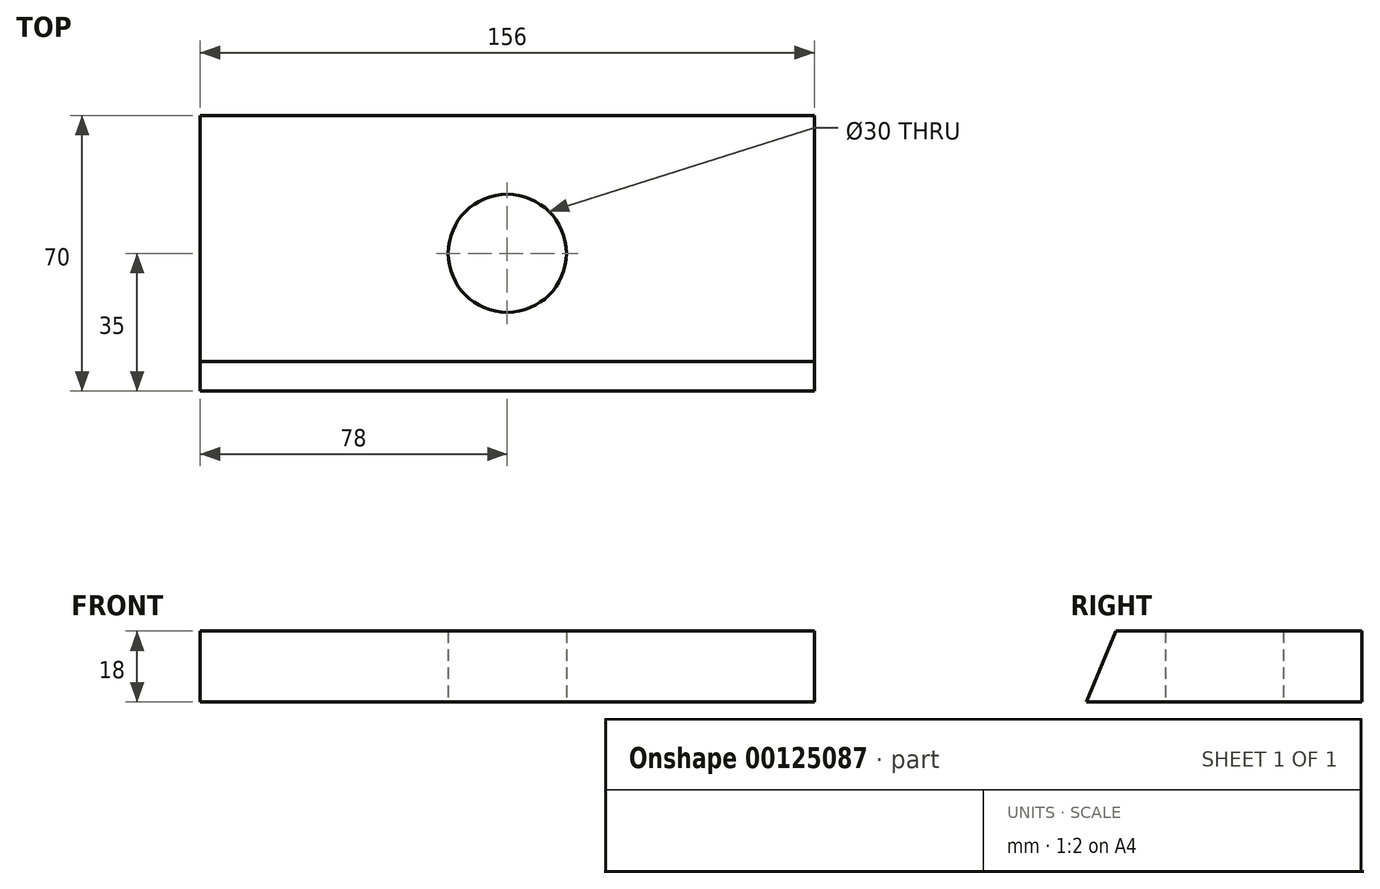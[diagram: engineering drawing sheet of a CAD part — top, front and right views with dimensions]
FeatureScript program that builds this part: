
annotation { "Feature Type Name" : "Feature", "Feature Type Description" : "" }
export const myFeature = defineFeature(function(context is Context, id is Id, definition is map)
    precondition{}
    {
        {
            var Q0;
            Q0=qCreatedBy(makeId("Top.planeOp"),FACE);
            var sketch = newSketch(context, id + "F0", { "sketchPlane" : qUnion([Q0])});
            skLineSegment(sketch, "E0.bottom", {"start": v(0, 0) * mm, "end": v(156, 0) * mm});
            skLineSegment(sketch, "E0.top", {"start": v(0, -70) * mm, "end": v(156, -70) * mm});
            skLineSegment(sketch, "E0.left", {"start": v(0, 0) * mm, "end": v(0, -70) * mm});
            skLineSegment(sketch, "E0.right", {"start": v(156, 0) * mm, "end": v(156, -70) * mm});
            skLineSegment(sketch, "E1", {"start": v(0, 0) * mm, "end": v(156, -70) * mm, "construction": true});
            skLineSegment(sketch, "E2", {"start": v(156, 0) * mm, "end": v(0, -70) * mm, "construction": true});
            skCircle(sketch, "E3", {"center": v(78, -35) * mm, "radius": 15 * mm});
            skSolve(sketch);
        }
        {
            var Q0;
            Q0=makeQuery(id+"F0.imprint","IMPRINT",FACE,{"disambiguationData":[TD([[makeQuery(id+"F0.imprint","IMPRINT",EDGE,{"derivedFrom":sQuery(id+"F0.wireOp",EDGE,"E0.bottom")}),-1.0]])]});
            extrude(context, id + "F1", {"entities" : qUnion([Q0]), "depth" : 18 * mm});
        }
        {
            var Q0;
            Q0=qCreatedBy(makeId("Right.planeOp"),FACE);
            var sketch = newSketch(context, id + "F2", { "sketchPlane" : qUnion([Q0])});
            skLineSegment(sketch, "E4.0.0", {"start": v(-70, 0) * mm, "end": v(0, 0) * mm});
            skLineSegment(sketch, "E4.0.1", {"start": v(0, 0) * mm, "end": v(0, 18) * mm});
            skLineSegment(sketch, "E4.0.2", {"start": v(0, 18) * mm, "end": v(-70, 18) * mm});
            skLineSegment(sketch, "E4.0.3", {"start": v(-70, 18) * mm, "end": v(-70, 0) * mm});
            skLineSegment(sketch, "E5", {"start": v(132, 0) * mm, "end": v(132, -188) * mm, "construction": true});
            skLineSegment(sketch, "E6", {"start": v(132, -188) * mm, "end": v(-148, -188) * mm, "construction": true});
            skLineSegment(sketch, "E7", {"start": v(-148, -188) * mm, "end": v(-70, 0) * mm, "construction": true});
            skLineSegment(sketch, "E8", {"start": v(-70, 0) * mm, "end": v(-62.53, 18) * mm, "construction": true});
            skLineSegment(sketch, "E9", {"start": v(-0.8, 18) * mm, "end": v(-62.53, 18) * mm, "construction": true});
            skLineSegment(sketch, "E10", {"start": v(-70, 0) * mm, "end": v(-62.53, 18) * mm});
            skLineSegment(sketch, "E11", {"start": v(-62.53, 18) * mm, "end": v(-70, 18) * mm});
            skLineSegment(sketch, "E12", {"start": v(0, 0) * mm, "end": v(132, 0) * mm, "construction": true});
            skSolve(sketch);
        }
        {
            var Q0;
            Q0=makeQuery(id+"F2.imprint","IMPRINT",FACE,{"disambiguationData":[TD([[makeQuery(id+"F2.imprint","IMPRINT",EDGE,{"derivedFrom":sQuery(id+"F2.wireOp",EDGE,"E4.0.3")}),1.0]])]});
            extrude(context, id + "F3", {"entities" : qUnion([Q0]), "operationType" : NewBodyOperationType.REMOVE, "depth" : 156 * mm});
        }
    });
